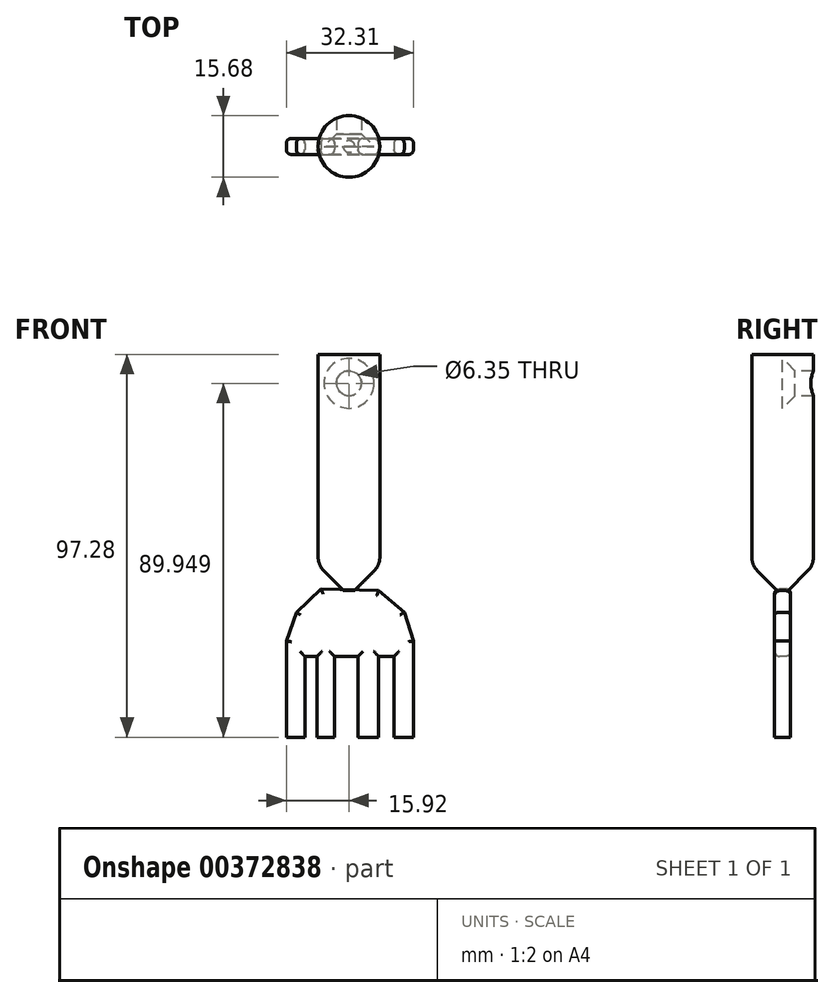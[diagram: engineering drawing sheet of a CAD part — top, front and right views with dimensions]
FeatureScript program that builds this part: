
annotation { "Feature Type Name" : "Feature", "Feature Type Description" : "" }
export const myFeature = defineFeature(function(context is Context, id is Id, definition is map)
    precondition{}
    {
        {
            var Q0;
            Q0=qCreatedBy(makeId("Front.planeOp"),FACE);
            var sketch = newSketch(context, id + "F0", { "sketchPlane" : qUnion([Q0])});
            skLineSegment(sketch, "E0", {"start": v(0, 50.18) * mm, "end": v(0, -9.73) * mm});
            skLineSegment(sketch, "E1", {"start": v(0, -9.73) * mm, "end": v(-7.84, -9.73) * mm});
            skLineSegment(sketch, "E2", {"start": v(-7.84, -9.73) * mm, "end": v(-7.84, 50.18) * mm});
            skLineSegment(sketch, "E3", {"start": v(-7.84, 50.18) * mm, "end": v(0, 50.18) * mm});
            skSolve(sketch);
        }
        {
            var Q0;
            Q0=makeQuery(id+"F0.imprint","IMPRINT",FACE,{"disambiguationData":[TD([[makeQuery(id+"F0.imprint","IMPRINT",EDGE,{"derivedFrom":sQuery(id+"F0.wireOp",EDGE,"E0")}),-1.0]])]});
            var Q1;
            Q1=sQuery(id+"F0.wireOp",EDGE,"E0");
            revolve(context, id + "F1", {"entities" : qUnion([Q0]), "axis" : qUnion([Q1]), "revolveType" : RevolveType.FULL});
        }
        {
            var Q0;
            Q0=qCreatedBy(makeId("Front.planeOp"),FACE);
            var sketch = newSketch(context, id + "F2", { "sketchPlane" : qUnion([Q0])});
            skLineSegment(sketch, "E4", {"start": v(-7.1, -9.35) * mm, "end": v(-13.38, -15.31) * mm});
            skLineSegment(sketch, "E5", {"start": v(-13.38, -15.31) * mm, "end": v(-15.92, -22.6) * mm});
            skLineSegment(sketch, "E6", {"start": v(-15.92, -22.6) * mm, "end": v(-15.92, -29.38) * mm});
            skLineSegment(sketch, "E7", {"start": v(-15.92, -29.38) * mm, "end": v(-15.92, -41.11) * mm});
            skLineSegment(sketch, "E8", {"start": v(-15.92, -41.11) * mm, "end": v(-15.92, -47.1) * mm});
            skLineSegment(sketch, "E9", {"start": v(-15.92, -47.1) * mm, "end": v(-11.23, -47.1) * mm});
            skLineSegment(sketch, "E10", {"start": v(-11.23, -47.1) * mm, "end": v(-11.23, -26.52) * mm});
            skLineSegment(sketch, "E11", {"start": v(-11.23, -26.52) * mm, "end": v(-8.1, -26.52) * mm});
            skLineSegment(sketch, "E12", {"start": v(-8.1, -26.52) * mm, "end": v(-8.1, -47.1) * mm});
            skLineSegment(sketch, "E13", {"start": v(-8.1, -47.1) * mm, "end": v(-3.67, -47.1) * mm});
            skLineSegment(sketch, "E14", {"start": v(-3.67, -47.1) * mm, "end": v(-3.67, -26.52) * mm});
            skLineSegment(sketch, "E15", {"start": v(-3.67, -26.52) * mm, "end": v(2.32, -26.52) * mm});
            skLineSegment(sketch, "E16", {"start": v(2.32, -26.52) * mm, "end": v(2.32, -47.1) * mm});
            skLineSegment(sketch, "E17", {"start": v(2.32, -47.1) * mm, "end": v(7.53, -47.1) * mm});
            skLineSegment(sketch, "E18", {"start": v(7.53, -47.1) * mm, "end": v(7.53, -26.52) * mm});
            skLineSegment(sketch, "E19", {"start": v(7.53, -26.52) * mm, "end": v(11.44, -26.52) * mm});
            skLineSegment(sketch, "E20", {"start": v(11.44, -26.52) * mm, "end": v(11.44, -47.1) * mm});
            skLineSegment(sketch, "E21", {"start": v(11.44, -47.1) * mm, "end": v(16.4, -47.1) * mm});
            skLineSegment(sketch, "E22", {"start": v(16.4, -47.1) * mm, "end": v(16.4, -26.52) * mm});
            skLineSegment(sketch, "E23", {"start": v(16.4, -26.52) * mm, "end": v(16.4, -22.6) * mm});
            skLineSegment(sketch, "E24", {"start": v(16.4, -22.6) * mm, "end": v(14.05, -15.31) * mm});
            skLineSegment(sketch, "E25", {"start": v(14.05, -15.31) * mm, "end": v(7.53, -9.84) * mm});
            skLineSegment(sketch, "E26", {"start": v(7.53, -9.84) * mm, "end": v(-7.1, -9.35) * mm});
            skSolve(sketch);
        }
        {
            var Q0;
            Q0 = qSketchRegion(id + "F2", true);
            extrude(context, id + "F3", {"entities" : qUnion([Q0]), "endBound" : BoundingType.SYMMETRIC, "oppositeDirection" : true, "depth" : 4.06 * mm});
        }
        {
            var Q0;
            Q0=makeQuery(id+"F1.opRevolve","SWEPT_EDGE",EDGE,{"disambiguationData":[OSD([sQuery(id+"F0.wireOp",EDGE,"E1"),sQuery(id+"F0.wireOp",EDGE,"E2")])]});
            chamfer(context, id + "F4", {"entities" : qUnion([Q0]), "width" : 6.35 * mm, "tangentPropagation" : true});
        }
        {
            var Q0;
            {var subQ0=sQuery(id+"F0.wireOp",EDGE,"E2");Q0=makeQuery(id+"F4.opChamfer","BLEND_EDGE",EDGE,{"blendedFrom":[makeQuery(id+"F1.opRevolve","SWEPT_EDGE",EDGE,{"disambiguationData":[OSD([sQuery(id+"F0.wireOp",EDGE,"E1"),subQ0])]}),makeQuery(id+"F1.opRevolve","SWEPT_FACE",FACE,{"disambiguationData":[OSD([subQ0])]})],"blendedInto":[makeQuery(id+"F1.opRevolve","SWEPT_FACE",FACE,{"disambiguationData":[OSD([subQ0])]})]});}
            fillet(context, id + "F5", {"entities" : qUnion([Q0]), "radius" : 5.08 * mm, "tangentPropagation" : true, "allowEdgeOverflow" : false});
        }
        {
            var Q0;
            Q0=makeQuery(id+"F3.opExtrude","CAP_EDGE",EDGE,{"disambiguationData":[OSD([sQuery(id+"F2.wireOp",EDGE,"E25")])],"isStart":false});
            var Q1;
            Q1=makeQuery(id+"F3.opExtrude","CAP_EDGE",EDGE,{"disambiguationData":[OSD([sQuery(id+"F2.wireOp",EDGE,"E24")])],"isStart":false});
            var Q2;
            Q2=makeQuery(id+"F3.opExtrude","CAP_EDGE",EDGE,{"disambiguationData":[OSD([sQuery(id+"F2.wireOp",EDGE,"E22"),sQuery(id+"F2.wireOp",EDGE,"E23")])],"isStart":false});
            var Q3;
            Q3=makeQuery(id+"F3.opExtrude","CAP_EDGE",EDGE,{"disambiguationData":[OSD([sQuery(id+"F2.wireOp",EDGE,"E20")])],"isStart":false});
            var Q4;
            Q4=makeQuery(id+"F3.opExtrude","CAP_EDGE",EDGE,{"disambiguationData":[OSD([sQuery(id+"F2.wireOp",EDGE,"E18")])],"isStart":false});
            var Q5;
            Q5=makeQuery(id+"F3.opExtrude","CAP_EDGE",EDGE,{"disambiguationData":[OSD([sQuery(id+"F2.wireOp",EDGE,"E19")])],"isStart":false});
            var Q6;
            Q6=makeQuery(id+"F3.opExtrude","CAP_EDGE",EDGE,{"disambiguationData":[OSD([sQuery(id+"F2.wireOp",EDGE,"E16")])],"isStart":false});
            var Q7;
            Q7=makeQuery(id+"F3.opExtrude","CAP_EDGE",EDGE,{"disambiguationData":[OSD([sQuery(id+"F2.wireOp",EDGE,"E15")])],"isStart":false});
            var Q8;
            Q8=makeQuery(id+"F3.opExtrude","CAP_EDGE",EDGE,{"disambiguationData":[OSD([sQuery(id+"F2.wireOp",EDGE,"E14")])],"isStart":false});
            var Q9;
            Q9=makeQuery(id+"F3.opExtrude","CAP_EDGE",EDGE,{"disambiguationData":[OSD([sQuery(id+"F2.wireOp",EDGE,"E12")])],"isStart":false});
            var Q10;
            Q10=makeQuery(id+"F3.opExtrude","CAP_EDGE",EDGE,{"disambiguationData":[OSD([sQuery(id+"F2.wireOp",EDGE,"E10")])],"isStart":false});
            var Q11;
            Q11=makeQuery(id+"F3.opExtrude","CAP_EDGE",EDGE,{"disambiguationData":[OSD([sQuery(id+"F2.wireOp",EDGE,"E11")])],"isStart":false});
            var Q12;
            Q12=makeQuery(id+"F3.opExtrude","CAP_EDGE",EDGE,{"disambiguationData":[OSD([sQuery(id+"F2.wireOp",EDGE,"E6"),sQuery(id+"F2.wireOp",EDGE,"E7"),sQuery(id+"F2.wireOp",EDGE,"E8")])],"isStart":false});
            var Q13;
            Q13=makeQuery(id+"F3.opExtrude","CAP_EDGE",EDGE,{"disambiguationData":[OSD([sQuery(id+"F2.wireOp",EDGE,"E5")])],"isStart":false});
            var Q14;
            Q14=makeQuery(id+"F3.opExtrude","CAP_EDGE",EDGE,{"disambiguationData":[OSD([sQuery(id+"F2.wireOp",EDGE,"E4")])],"isStart":false});
            var Q15;
            Q15=makeQuery(id+"F3.opExtrude","CAP_EDGE",EDGE,{"disambiguationData":[OSD([sQuery(id+"F2.wireOp",EDGE,"E26")])],"isStart":false});
            var Q16;
            Q16=makeQuery(id+"F3.opExtrude","CAP_EDGE",EDGE,{"disambiguationData":[OSD([sQuery(id+"F2.wireOp",EDGE,"E24")])],"isStart":true});
            var Q17;
            Q17=makeQuery(id+"F3.opExtrude","CAP_EDGE",EDGE,{"disambiguationData":[OSD([sQuery(id+"F2.wireOp",EDGE,"E22"),sQuery(id+"F2.wireOp",EDGE,"E23")])],"isStart":true});
            var Q18;
            Q18=makeQuery(id+"F3.opExtrude","CAP_EDGE",EDGE,{"disambiguationData":[OSD([sQuery(id+"F2.wireOp",EDGE,"E20")])],"isStart":true});
            var Q19;
            Q19=makeQuery(id+"F3.opExtrude","CAP_EDGE",EDGE,{"disambiguationData":[OSD([sQuery(id+"F2.wireOp",EDGE,"E18")])],"isStart":true});
            var Q20;
            Q20=makeQuery(id+"F3.opExtrude","CAP_EDGE",EDGE,{"disambiguationData":[OSD([sQuery(id+"F2.wireOp",EDGE,"E19")])],"isStart":true});
            var Q21;
            Q21=makeQuery(id+"F3.opExtrude","CAP_EDGE",EDGE,{"disambiguationData":[OSD([sQuery(id+"F2.wireOp",EDGE,"E25")])],"isStart":true});
            var Q22;
            Q22=makeQuery(id+"F3.opExtrude","CAP_EDGE",EDGE,{"disambiguationData":[OSD([sQuery(id+"F2.wireOp",EDGE,"E26")])],"isStart":true});
            var Q23;
            Q23=makeQuery(id+"F3.opExtrude","CAP_EDGE",EDGE,{"disambiguationData":[OSD([sQuery(id+"F2.wireOp",EDGE,"E4")])],"isStart":true});
            var Q24;
            Q24=makeQuery(id+"F3.opExtrude","CAP_EDGE",EDGE,{"disambiguationData":[OSD([sQuery(id+"F2.wireOp",EDGE,"E5")])],"isStart":true});
            var Q25;
            Q25=makeQuery(id+"F3.opExtrude","CAP_EDGE",EDGE,{"disambiguationData":[OSD([sQuery(id+"F2.wireOp",EDGE,"E6"),sQuery(id+"F2.wireOp",EDGE,"E7"),sQuery(id+"F2.wireOp",EDGE,"E8")])],"isStart":true});
            var Q26;
            Q26=makeQuery(id+"F3.opExtrude","CAP_EDGE",EDGE,{"disambiguationData":[OSD([sQuery(id+"F2.wireOp",EDGE,"E10")])],"isStart":true});
            var Q27;
            Q27=makeQuery(id+"F3.opExtrude","CAP_EDGE",EDGE,{"disambiguationData":[OSD([sQuery(id+"F2.wireOp",EDGE,"E11")])],"isStart":true});
            var Q28;
            Q28=makeQuery(id+"F3.opExtrude","CAP_EDGE",EDGE,{"disambiguationData":[OSD([sQuery(id+"F2.wireOp",EDGE,"E12")])],"isStart":true});
            var Q29;
            Q29=makeQuery(id+"F3.opExtrude","CAP_EDGE",EDGE,{"disambiguationData":[OSD([sQuery(id+"F2.wireOp",EDGE,"E15")])],"isStart":true});
            var Q30;
            Q30=makeQuery(id+"F3.opExtrude","CAP_EDGE",EDGE,{"disambiguationData":[OSD([sQuery(id+"F2.wireOp",EDGE,"E16")])],"isStart":true});
            var Q31;
            Q31=makeQuery(id+"F3.opExtrude","CAP_EDGE",EDGE,{"disambiguationData":[OSD([sQuery(id+"F2.wireOp",EDGE,"E14")])],"isStart":true});
            fillet(context, id + "F6", {"entities" : qUnion([Q0, Q1, Q2, Q3, Q4, Q5, Q6, Q7, Q8, Q9, Q10, Q11, Q12, Q13, Q14, Q15, Q16, Q17, Q18, Q19, Q20, Q21, Q22, Q23, Q24, Q25, Q26, Q27, Q28, Q29, Q30, Q31]), "radius" : 1.27 * mm, "tangentPropagation" : true, "allowEdgeOverflow" : false});
        }
        {
            var Q0;
            Q0=qCreatedBy(makeId("Front.planeOp"),FACE);
            var sketch = newSketch(context, id + "F7", { "sketchPlane" : qUnion([Q0])});
            skLineSegment(sketch, "E27", {"start": v(0, 42.85) * mm, "end": v(-3.67, 38.05) * mm});
            skLineSegment(sketch, "E28", {"start": v(-3.67, 38.05) * mm, "end": v(0, 35.25) * mm});
            skLineSegment(sketch, "E29", {"start": v(0, 35.25) * mm, "end": v(4.68, 38.05) * mm});
            skLineSegment(sketch, "E30", {"start": v(4.68, 38.05) * mm, "end": v(0, 42.85) * mm});
            skSolve(sketch);
        }
        {
            var Q0;
            Q0=sQuery(id+"F7.wireOp",VERTEX,"E30.end");
            var Q1;
            Q1=makeQuery(id+"F1.opRevolve","SWEPT_BODY",BODY,{"disambiguationData":[OSD([sQuery(id+"F0.wireOp",EDGE,"E0"),sQuery(id+"F0.wireOp",EDGE,"E1"),sQuery(id+"F0.wireOp",EDGE,"E2"),sQuery(id+"F0.wireOp",EDGE,"E3"),sQuery(id+"F0.wireOp",EDGE,"6OIuukLd-o3Wf-8uIs-GKxZ-Eo16lnFXZqOb"),sQuery(id+"F0.wireOp",EDGE,"KNn3lmPw-eaZM-QG9M-C7zM-d8kRAE3bGZ97")])]});
            hole(context, id + "F8", {"style" : HoleStyle.C_SINK, "endStyle" : HoleEndStyle.THROUGH, "holeDiameter" : 6.35 * mm, "cSinkDiameter" : 12.7 * mm, "cSinkAngle" : 90 * degree, "isTappedThrough" : true, "tappedDepth" : 12.7 * mm, "tapClearance" : 3, "startFromSketch" : true, "locations" : qUnion([Q0]), "scope" : qUnion([Q1])});
        }
    });
